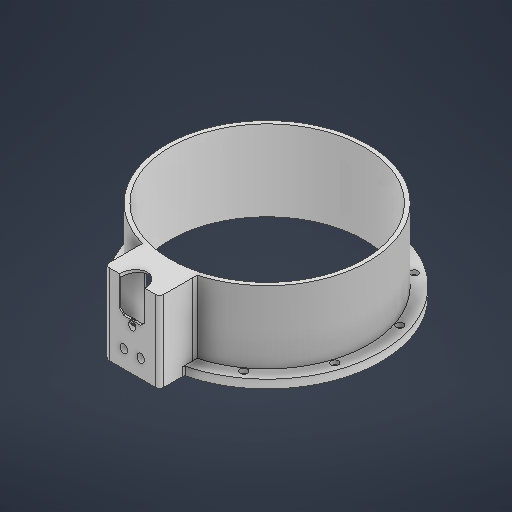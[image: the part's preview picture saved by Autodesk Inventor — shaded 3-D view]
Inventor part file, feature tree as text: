
AUTODESK INVENTOR PART (.ipt)
format: ipt  version: 2025 (Build 290162000, 162)  size: 611,328 bytes
history: native  units: in
note: dims shown in document units (in); Inventor stores cm internally (conversion verified against a paired STEP export)
features: extrude x22, sketch x19, fillet x4, other x3, plane x3, chamfer x2
ambient origin geometry x8: Origin, YZ Plane, XZ Plane, XY Plane, X Axis, Y Axis, Z Axis, Center Point
bodies: Body1 (feature_tree)
feature tree (53):
  other  "Cylinder.ipt"
  extrude  "Extrusion1"  Depth=0.3937in
  extrude  "Extrusion2"  Depth=0.3937in TaperAngle=0.0deg
  sketch  "Sketch3"  dims[d7=11.2205in d8=10.6299in]
  extrude  "Extrusion3"  Depth=10.6299in
  extrude  "Extrusion5"  Depth=0.1969in TaperAngle=0.0deg
  sketch  "Sketch6"  dims[d24=0.1969in d25=0.0in d31=0.0in d32=0.0in]
  extrude  "Extrusion6"  Depth=10.6299in
  extrude  "Extrusion7"  TaperAngle=0.0deg  [1 undecoded]
  extrude  "Extrusion8"  Depth=2.1654in
  plane  "Work Plane1"
  extrude  "Extrusion9"  Depth=9.065in
  extrude  "Extrusion21"  Depth=0.0787in
  sketch  "Sketch19"  dims[d107=2.2047in d108=0.0in d113=2.5591in]
  extrude  "Extrusion23"  Depth=2.5591in
  extrude  "Extrusion27"  Depth=0.0591in
  extrude  "Extrusion33"  Depth=0.5433in
  extrude  "Extrusion34"  Depth=0.0787in
  fillet  "Fillet10"  Radius=0.3937in
  fillet  "Fillet12"  Radius=1.5298in
  extrude  "Extrusion36"  Depth=0.0787in
  extrude  "Extrusion40"  Depth=4.1339in TaperAngle=0.0deg
  extrude  "Extrusion42"  Depth=0.0787in
  fillet  "Fillet19"  Radius=0.0787in
  fillet  "Fillet20"  Radius=0.1969in
  sketch  "Sketch30"  dims[d122=9.4488in d134=0.0787in d141=0.3937in d142=0.0in d164=1.5298in]
  sketch  "Sketch31"  dims[d165=0.0787in d166=1.8325in]
  extrude  "Extrusion44"  Depth=0.2165in
  chamfer  "Chamfer8"  Distance=3.937in Angle=360.0deg
  extrude  "Extrusion57"  Depth=9.065in
  extrude  "Extrusion58"  Depth=0.3937in TaperAngle=0.0deg
  plane  "Work Plane2"
  extrude  "Extrusion59"  Depth=0.1969in
  extrude  "Extrusion61"  Depth=0.1969in
  plane  "Work Plane3"
  extrude  "Extrusion63"  Depth=0.1969in
  chamfer  "Chamfer10"  Distance=2.564in
  other  "Solid12::Cylinder.ipt"
  other  "TaggingFeature1"
  sketch  "Sketch1"  dims[d0=0.3937in d2=10.2362in]
  sketch  "Sketch2"  dims[d3=0.0in d4=0.0in d5=0.3937in d6=0.0in]
  sketch  "Sketch5"  dims[d17=10.6299in d18=0.2953in]
  sketch  "Sketch7"  dims[d33=2.1654in d34=0.0in d35=9.8425in]
  sketch  "Sketch9"  dims[d36=10.6299in d46=9.065in]
  sketch  "Sketch14"  dims[d47=0.3937in d48=0.0in d88=0.0787in]
  sketch  "Sketch22"  dims[d115=2.2047in d116=0.0in d117=0.0591in]
  sketch  "Sketch24"  dims[d119=0.5433in d120=0.5433in]
  sketch  "Sketch Circular Pattern3"  dims[d10=0.1969in d11=0.0in d15=0.1969in d16=0.0in]
  sketch  "Sketch45"  dims[d167=90.0deg d171=4.1339in d172=0.0in]
  sketch  "Sketch47"  dims[d173=1.1614in d174=0.0in d175=0.0787in d178=0.0787in d180=0.1969in]
  sketch  "Sketch48"  dims[d189=3.0541in d190=0.0in d209=0.2165in]
  sketch  "Sketch50"  dims[d210=0.3425in d211=3.937in d213=360.0deg]
  sketch  "Sketch52"  dims[d217=10.4151in d218=9.065in d221=0.3937in d222=0.0in d223=0.5433in d224=1.8228in d225=3.5433in d226=2.564in d227=2.7608in d228=3.5433in d233=1.9291in d234=0.0in d235=0.1969in d236=0.9916in d237=0.0in d238=0.1969in d246=2.1654in d247=0.0in d248=1.0787in d249=1.6412in d250=45.0deg d267=1.1811in d268=0.0787in d269=0.0787in d270=0.0787in d271=0.0443in d317=0.3346in d318=0.0in d319=0.0in d320=0.3346in d321=0.3346in d322=0.3937in d323=0.3937in d324=0.9055in d325=0.9055in d326=0.1575in d327=0.1575in d328=0.1575in d329=0.1575in d330=0.0in d331=0.8474in d334=0.9675in d335=0.0in d336=1.1811in d340=1.1778in d341=0.9675in d342=0.0in d346=3.3526in d347=1.4567in d348=0.5709in d349=1.1024in d350=0.0in d351=0.1969in d352=0.2037in d353=45.0deg d143=0.0197in d144=0.0344in d145=0.0197in d146=0.0344in d153=0.0in d154=0.0in d155=0.0in d156=0.0in d201=0.0197in d202=0.0344in d203=0.0197in d204=0.0344in d215=0.0197in d216=0.0344in d252=0.0197in d253=0.0344in d254=0.0197in d255=0.0344in d304=0.0197in d305=0.0344in d306=0.0197in d307=0.0344in]
note: 1 required parameter value undecoded (feature->parameter linkage not recoverable at this tier; creation-order binding heuristic only, values carry confidence <= 0.55)
